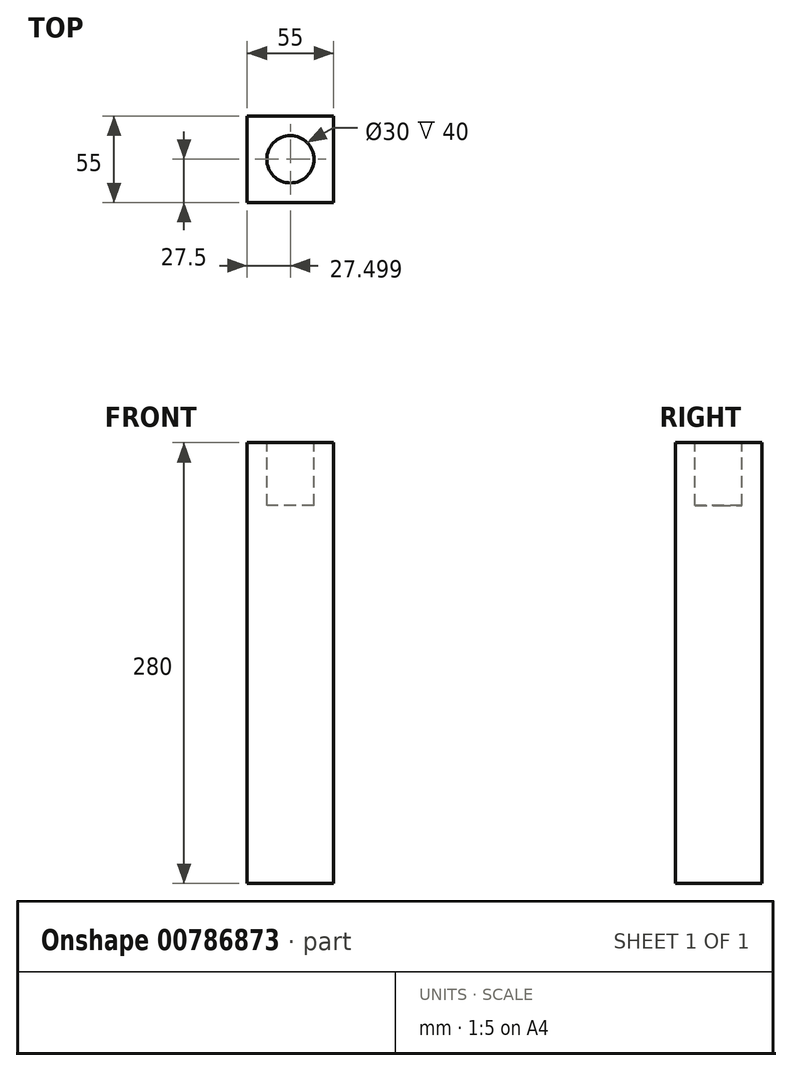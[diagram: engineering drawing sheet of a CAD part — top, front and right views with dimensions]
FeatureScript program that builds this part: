
annotation { "Feature Type Name" : "Feature", "Feature Type Description" : "" }
export const myFeature = defineFeature(function(context is Context, id is Id, definition is map)
    precondition{}
    {
        {
            var Q0;
            Q0=qCreatedBy(makeId("Top.planeOp"),FACE);
            var sketch = newSketch(context, id + "F0", { "sketchPlane" : qUnion([Q0])});
            skLineSegment(sketch, "E0.bottom", {"start": v(-72.27, 35.78) * mm, "end": v(-17.27, 35.78) * mm});
            skLineSegment(sketch, "E0.top", {"start": v(-72.27, -19.22) * mm, "end": v(-17.27, -19.22) * mm});
            skLineSegment(sketch, "E0.left", {"start": v(-72.27, 35.78) * mm, "end": v(-72.27, -19.22) * mm});
            skLineSegment(sketch, "E0.right", {"start": v(-17.27, 35.78) * mm, "end": v(-17.27, -19.22) * mm});
            skLineSegment(sketch, "E1", {"start": v(-72.27, 35.78) * mm, "end": v(-17.27, -19.22) * mm, "construction": true});
            skLineSegment(sketch, "E2", {"start": v(-72.27, -19.22) * mm, "end": v(-17.27, 35.78) * mm, "construction": true});
            skSolve(sketch);
        }
        {
            var Q0;
            Q0 = qSketchRegion(id + "F0", true);
            extrude(context, id + "F1", {"entities" : qUnion([Q0]), "depth" : 280 * mm, "offsetDistance" : 25 * mm});
        }
        {
            var Q0;
            Q0=makeQuery(id+"F1.opExtrude","CAP_FACE",FACE,{"disambiguationData":[OSD([sQuery(id+"F0.wireOp",EDGE,"E0.bottom"),sQuery(id+"F0.wireOp",EDGE,"E0.top"),sQuery(id+"F0.wireOp",EDGE,"E0.left"),sQuery(id+"F0.wireOp",EDGE,"E0.right")])],"isStart":false});
            var sketch = newSketch(context, id + "F2", { "sketchPlane" : qUnion([Q0])});
            skLineSegment(sketch, "E3", {"start": v(-72.27, 35.78) * mm, "end": v(-17.27, -19.22) * mm, "construction": true});
            skLineSegment(sketch, "E4", {"start": v(-17.27, 35.78) * mm, "end": v(-72.27, -19.22) * mm, "construction": true});
            skCircle(sketch, "E5", {"center": v(-44.77, 8.28) * mm, "radius": 15 * mm});
            skSolve(sketch);
        }
        {
            var Q0;
            Q0 = qSketchRegion(id + "F2", true);
            var Q1;
            Q1=sQuery(id+"F2.wireOp",EDGE,"E5");
            extrude(context, id + "F3", {"entities" : qUnion([Q0]), "operationType" : NewBodyOperationType.REMOVE, "surfaceEntities" : qUnion([Q1]), "oppositeDirection" : true, "depth" : 40 * mm, "offsetDistance" : 25 * mm});
        }
    });
